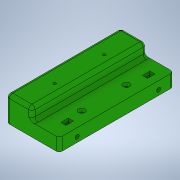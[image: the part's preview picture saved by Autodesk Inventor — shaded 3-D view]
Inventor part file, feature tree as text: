
AUTODESK INVENTOR PART (.ipt)
format: ipt  version: 2020 (Build 240168000, 168)  size: 295,424 bytes
history: native  units: in
note: dims shown in document units (in); Inventor stores cm internally (conversion verified against a paired STEP export)
features: extrude x7, sketch x7, other x6, reference x4, fillet x2, chamfer x1, projected_geometry x1
ambient origin geometry x8: Origin, YZ Plane, XZ Plane, XY Plane, X Axis, Y Axis, Z Axis, Center Point
bodies: Body1 (feature_tree)
feature tree (28):
  other  "Твердое тело1"
  extrude  "Выдавливание1"  Depth=0.1181in TaperAngle=0.0deg
  extrude  "Выдавливание2"  Depth=0.1181in TaperAngle=0.0deg
  sketch  "Эскиз3"
  other  "РабПлоскость1"
  extrude  "Выдавливание3"  Depth=0.1181in TaperAngle=0.0deg
  other  "Толщина1"
  fillet  "Сопряжение1"  Radius=0.1in
  extrude  "Выдавливание4"  Depth=0.1in
  fillet  "Сопряжение2"  Radius=0.125in
  chamfer  "Фаска1"  Distance=0.315in
  extrude  "Выдавливание5"  Depth=0.315in
  extrude  "Выдавливание6"  Depth=0.3937in TaperAngle=0.0deg
  extrude  "Выдавливание7"  Depth=0.125in
  sketch  "Эскиз2"
  reference  "Ссылка1"
  reference  "Ссылка2"
  reference  "Ссылка3"
  reference  "Ссылка4"
  sketch  "Эскиз4"
  sketch  "Эскиз5"
  projected_geometry  "Спроецированная петля1"
  sketch  "Эскиз6"
  sketch  "Эскиз7"
  sketch  "Эскиз1"
  other  "realsenses_plate_v2.ipt.iam"
  other  "Intel RealSense T265:1"
  other  "body:1"
